# Revit family: STH7707_30
name_source: partatom
category: Luminárias
units: mm (PartAtom-declared; Revit-internal decimal feet)

## family parameters
Compartilhado = Não
Corte com vazios quando carregada = Sim
Cota do conector redondo = Utilizar diâmetro
Fonte luminosa = Sim
Hospedeiro = Piso
Manter orientação da anotação = Não
Ponto de cálculo do ambiente = Não
Sempre na vertical = Sim
Tipo de parte = Normal

## types (1)
- STH7707/30 - BIVOLT
    Altura = 0 m
    Arquivo de rede fotométrica = STELLA - STH7707-30 - FOCCO 30° 10W.ies
    Dimerização = Não dimerizável
    Diâmetro = 0 m
    Elevação padrão = 0 m
    Estrutura = Al - Preto
    Fabricante = Stella
    Filtro de cor = 16777215
    Fluxo Luminoso = 640 lm
    Grau de proteção (IP) = IP67
    IRC (Índice de reprodução de cores) = >80
    Luminoso = Luminoso - 3000K
    Modelo = Focco 30°
    Potência = 10 W
    Referência = STH7707/30
    Silicone = Borracha Silicone
    Temperatura da cor (K) = 3000 K
    Tensão Elétrica = 100V-240V
    Troca de temperatura da cor de lâmpada com esmaecimento = <Nenhum>
    URL = https://stella.com.br
    Vidro = Vidro
    Ângulo de Abertura = 30°
    Ângulo de inclinação = -90.00°
